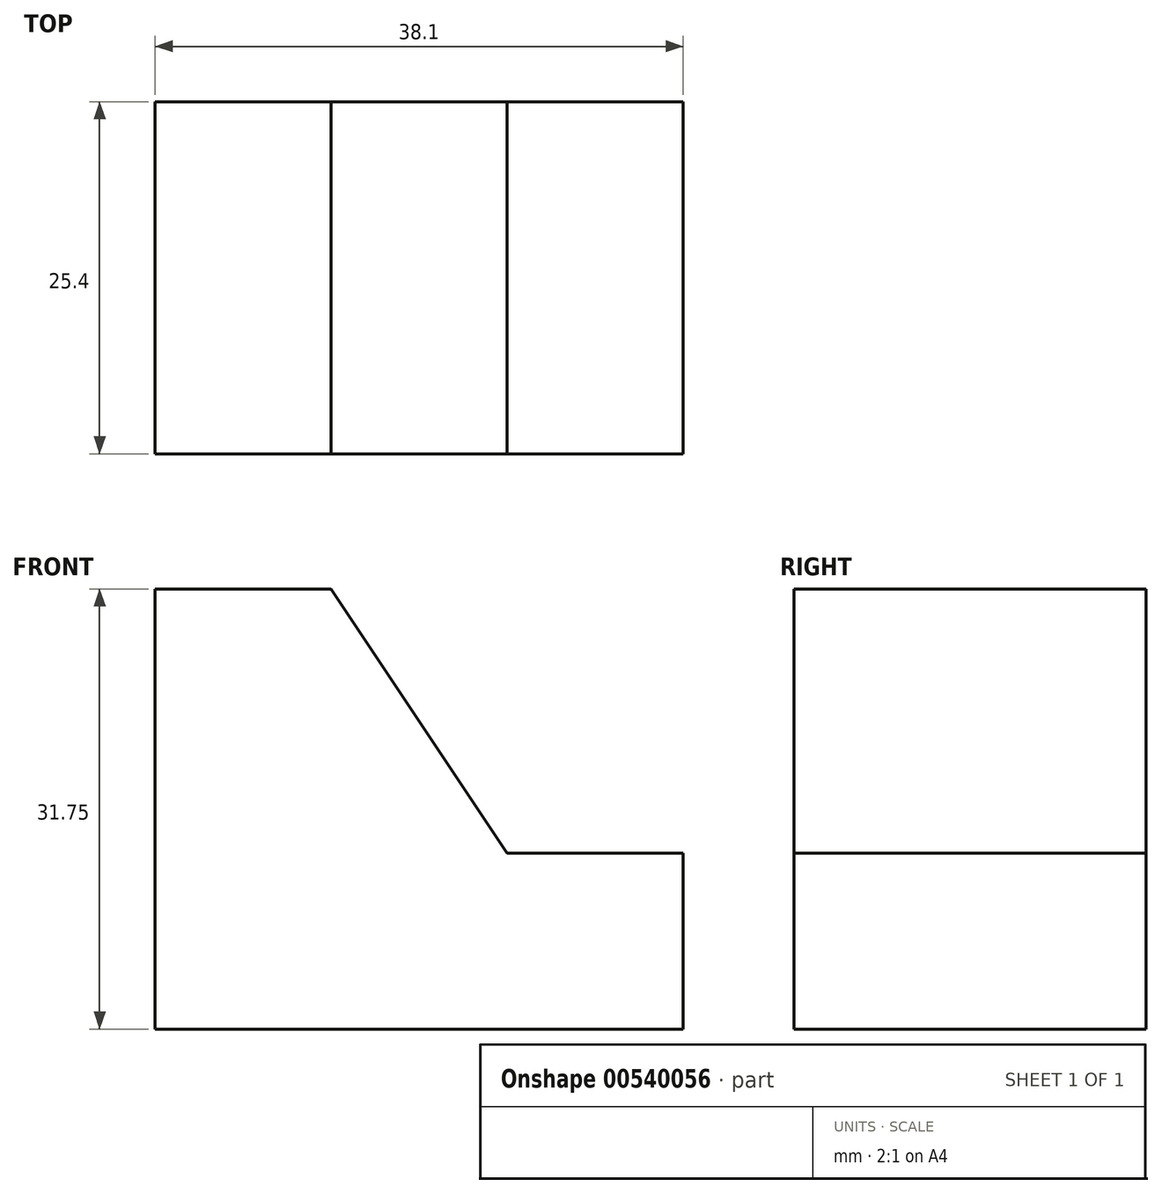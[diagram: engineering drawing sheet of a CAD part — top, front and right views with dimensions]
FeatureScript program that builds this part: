
annotation { "Feature Type Name" : "Feature", "Feature Type Description" : "" }
export const myFeature = defineFeature(function(context is Context, id is Id, definition is map)
    precondition{}
    {
        {
            var Q0;
            Q0=qCreatedBy(makeId("Front.planeOp"),FACE);
            var sketch = newSketch(context, id + "F0", { "sketchPlane" : qUnion([Q0])});
            skLineSegment(sketch, "E0", {"start": v(0, 0) * mm, "end": v(38.1, 0) * mm});
            skLineSegment(sketch, "E1", {"start": v(38.1, 0) * mm, "end": v(38.1, 31.75) * mm});
            skLineSegment(sketch, "E2", {"start": v(38.1, 31.75) * mm, "end": v(0, 31.75) * mm});
            skLineSegment(sketch, "E3", {"start": v(0, 31.75) * mm, "end": v(0, 0) * mm});
            skSolve(sketch);
        }
        {
            var Q0;
            Q0 = qSketchRegion(id + "F0", true);
            extrude(context, id + "F1", {"entities" : qUnion([Q0]), "depth" : 25.4 * mm, "offsetDistance" : 25.4 * mm});
        }
        {
            var Q0;
            Q0=makeQuery(id+"F1.opExtrude","CAP_FACE",FACE,{"disambiguationData":[OSD([sQuery(id+"F0.wireOp",EDGE,"E0"),sQuery(id+"F0.wireOp",EDGE,"E1"),sQuery(id+"F0.wireOp",EDGE,"E2"),sQuery(id+"F0.wireOp",EDGE,"E3")])],"isStart":false});
            var sketch = newSketch(context, id + "F2", { "sketchPlane" : qUnion([Q0])});
            skLineSegment(sketch, "E4", {"start": v(0, 31.75) * mm, "end": v(12.7, 31.75) * mm});
            skLineSegment(sketch, "E5", {"start": v(38.1, 0) * mm, "end": v(38.1, 12.7) * mm});
            skLineSegment(sketch, "E6", {"start": v(38.1, 12.7) * mm, "end": v(25.4, 12.7) * mm});
            skLineSegment(sketch, "E7", {"start": v(25.4, 12.7) * mm, "end": v(12.7, 31.75) * mm});
            skSolve(sketch);
        }
        {
            var Q0;
            Q0 = qSketchRegion(id + "F2", true);
            var Q1;
            {var subQ0=sQuery(id+"F2.wireOp",EDGE,"E6");Q1=makeQuery(id+"F2.imprint","IMPRINT",FACE,{"disambiguationData":[TD([[makeQuery(id+"F2.imprint","IMPRINT",EDGE,{"derivedFrom":subQ0}),-1.0]])]});}
            extrude(context, id + "F3", {"entities" : qUnion([Q0, Q1]), "operationType" : NewBodyOperationType.REMOVE, "oppositeDirection" : true, "depth" : 25.4 * mm, "offsetDistance" : 25.4 * mm});
        }
    });
